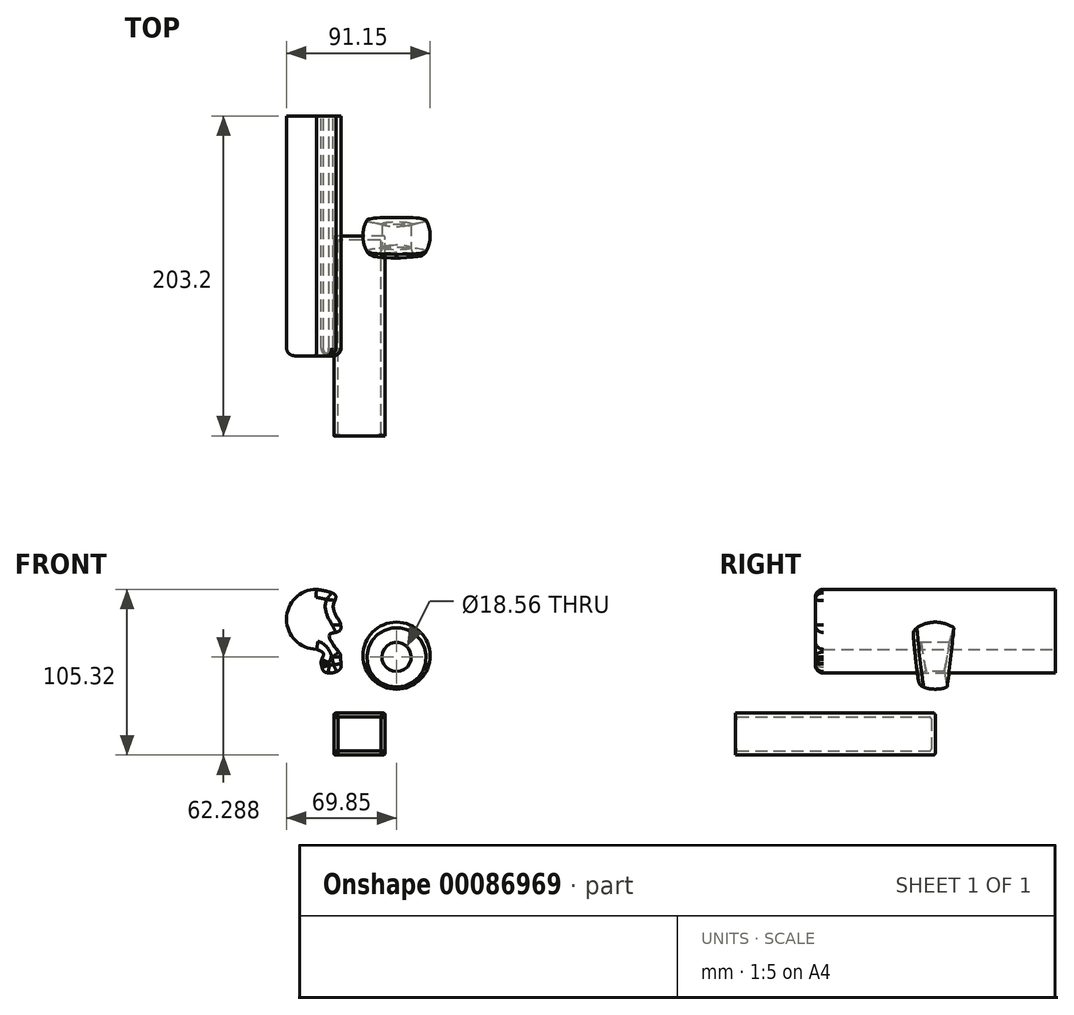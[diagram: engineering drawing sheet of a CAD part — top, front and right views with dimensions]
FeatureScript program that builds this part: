
annotation { "Feature Type Name" : "Feature", "Feature Type Description" : "" }
export const myFeature = defineFeature(function(context is Context, id is Id, definition is map)
    precondition{}
    {
        {
            var Q0;
            Q0=qCreatedBy(makeId("Front.planeOp"),FACE);
            var sketch = newSketch(context, id + "F0", { "sketchPlane" : qUnion([Q0])});
            skLineSegment(sketch, "E0", {"start": v(0, 0) * mm, "end": v(0, 42.6) * mm});
            skArc(sketch, "E1", {"start": v(0, 42.6) * mm, "mid": v(-21.3, 21.3) * mm, "end": v(0, 0) * mm});
            skSolve(sketch);
        }
        {
            var Q0;
            Q0 = qSketchRegion(id + "F0", true);
            var Q1;
            Q1=sQuery(id+"F0.wireOp",EDGE,"E0");
            revolve(context, id + "F1", {"entities" : qUnion([Q0]), "axis" : qUnion([Q1]), "revolveType" : RevolveType.FULL});
        }
        {
            var Q0;
            Q0=qCreatedBy(makeId("Front.planeOp"),FACE);
            var sketch = newSketch(context, id + "F2", { "sketchPlane" : qUnion([Q0])});
            skCircle(sketch, "E2", {"center": v(0, 20.47) * mm, "radius": 9.28 * mm});
            skSolve(sketch);
        }
        {
            var Q0;
            Q0 = qSketchRegion(id + "F2", true);
            extrude(context, id + "F3", {"entities" : qUnion([Q0]), "operationType" : NewBodyOperationType.REMOVE, "endBound" : BoundingType.SYMMETRIC, "oppositeDirection" : true, "depth" : 92.12 * mm});
        }
        {
            var Q0;
            Q0=qCreatedBy(makeId("Front.planeOp"),FACE);
            var sketch = newSketch(context, id + "F4", { "sketchPlane" : qUnion([Q0])});
            skArc(sketch, "E3", {"start": v(-50.8, 63.5) * mm, "mid": v(-69.85, 44.45) * mm, "end": v(-50.8, 25.4) * mm});
            skLineSegment(sketch, "E4", {"start": v(-50.8, 63.5) * mm, "end": v(-50.8, 25.4) * mm, "construction": true});
            skFitSpline(sketch, "E5", {"points": [v(-50.8, 63.5) * mm, v(-38.58, 59.25) * mm, v(-40.15, 53.18) * mm, v(-37.21, 44.75) * mm, v(-35.65, 41.62) * mm, v(-35.65, 37.7) * mm, v(-39.37, 35.94) * mm, v(-42.7, 34.18) * mm, v(-38, 25.36) * mm, v(-35.65, 22.03) * mm, v(-35.45, 18.5) * mm, v(-35.45, 13.42) * mm, v(-40.35, 10.48) * mm, v(-46.03, 11.26) * mm, v(-47.4, 14.2) * mm, v(-47.8, 18.12) * mm, v(-46.42, 22.43) * mm, v(-50.8, 25.4) * mm], "startDerivative": vector(187.17, -33.7) * mm, "endDerivative": vector(-104.87, 42.61) * mm});
            skSolve(sketch);
        }
        {
            var Q0;
            Q0 = qSketchRegion(id + "F4", true);
            extrude(context, id + "F5", {"entities" : qUnion([Q0]), "endBound" : BoundingType.SYMMETRIC, "depth" : 152.4 * mm});
        }
        {
            var Q0;
            Q0=makeQuery(id+"F5.opExtrude","CAP_EDGE",EDGE,{"disambiguationData":[OSD([sQuery(id+"F4.wireOp",EDGE,"E3")])],"isStart":false});
            var Q1;
            Q1=makeQuery(id+"F5.opExtrude","CAP_EDGE",EDGE,{"disambiguationData":[OSD([sQuery(id+"F4.wireOp",EDGE,"E5")])],"isStart":false});
            fillet(context, id + "F6", {"entities" : qUnion([Q0, Q1]), "radius" : 5.08 * mm, "tangentPropagation" : true, "allowEdgeOverflow" : false});
        }
        {
            var Q0;
            Q0=makeQuery(id+"F3.boolean.opBoolean","INTERSECT",EDGE,{"disambiguationData":[OD(1.0)],"derivedFrom":[makeQuery(id+"F1.opRevolve","SWEPT_FACE",FACE,{"disambiguationData":[OSD([sQuery(id+"F0.wireOp",EDGE,"E1")])]}),makeQuery(id+"F3.opExtrude","SWEPT_FACE",FACE,{"disambiguationData":[OSD([sQuery(id+"F2.wireOp",EDGE,"E2")])]})]});
            chamfer(context, id + "F7", {"entities" : qUnion([Q0]), "width" : 5.08 * mm, "tangentPropagation" : true});
        }
        {
            var Q0;
            Q0=makeQuery(id+"F3.boolean.opBoolean","INTERSECT",EDGE,{"disambiguationData":[OD(0.0)],"derivedFrom":[makeQuery(id+"F1.opRevolve","SWEPT_FACE",FACE,{"disambiguationData":[OSD([sQuery(id+"F0.wireOp",EDGE,"E1")])]}),makeQuery(id+"F3.opExtrude","SWEPT_FACE",FACE,{"disambiguationData":[OSD([sQuery(id+"F2.wireOp",EDGE,"E2")])]})]});
            fillet(context, id + "F8", {"entities" : qUnion([Q0]), "radius" : 5.08 * mm, "tangentPropagation" : true, "allowEdgeOverflow" : false});
        }
        {
            var Q0;
            Q0=qCreatedBy(makeId("Front.planeOp"),FACE);
            var sketch = newSketch(context, id + "F9", { "sketchPlane" : qUnion([Q0])});
            skLineSegment(sketch, "E6.bottom", {"start": v(-7.25, -15.18) * mm, "end": v(-39.76, -15.18) * mm});
            skLineSegment(sketch, "E6.top", {"start": v(-7.25, -41.82) * mm, "end": v(-39.76, -41.82) * mm});
            skLineSegment(sketch, "E6.left", {"start": v(-7.25, -15.18) * mm, "end": v(-7.25, -41.82) * mm});
            skLineSegment(sketch, "E6.right", {"start": v(-39.76, -15.18) * mm, "end": v(-39.76, -41.82) * mm});
            skPoint(sketch, "E6.middle", {"position": v(-23.5, -28.5) * mm});
            skSolve(sketch);
        }
        {
            var Q0;
            Q0 = qSketchRegion(id + "F9", true);
            extrude(context, id + "F10", {"entities" : qUnion([Q0]), "depth" : 127 * mm});
        }
        {
            var Q0;
            Q0=makeQuery(id+"F10.opExtrude","CAP_FACE",FACE,{"disambiguationData":[OSD([sQuery(id+"F9.wireOp",EDGE,"E6.bottom"),sQuery(id+"F9.wireOp",EDGE,"E6.top"),sQuery(id+"F9.wireOp",EDGE,"E6.left"),sQuery(id+"F9.wireOp",EDGE,"E6.right")])],"isStart":false});
            shell(context, id + "F11", {"entities" : qUnion([Q0]), "thickness" : 2.54 * mm});
        }
        {
            var Q0;
            Q0=makeQuery(id+"F10.opExtrude","SWEPT_EDGE",EDGE,{"disambiguationData":[OSD([sQuery(id+"F9.wireOp",EDGE,"E6.bottom"),sQuery(id+"F9.wireOp",EDGE,"E6.right")])]});
            var Q1;
            Q1=makeQuery(id+"F10.opExtrude","SWEPT_EDGE",EDGE,{"disambiguationData":[OSD([sQuery(id+"F9.wireOp",EDGE,"E6.top"),sQuery(id+"F9.wireOp",EDGE,"E6.right")])]});
            var Q2;
            Q2=makeQuery(id+"F10.opExtrude","SWEPT_EDGE",EDGE,{"disambiguationData":[OSD([sQuery(id+"F9.wireOp",EDGE,"E6.top"),sQuery(id+"F9.wireOp",EDGE,"E6.left")])]});
            var Q3;
            Q3=makeQuery(id+"F10.opExtrude","SWEPT_EDGE",EDGE,{"disambiguationData":[OSD([sQuery(id+"F9.wireOp",EDGE,"E6.bottom"),sQuery(id+"F9.wireOp",EDGE,"E6.left")])]});
            var Q4;
            {var subQ0=sQuery(id+"F9.wireOp",EDGE,"E6.right");Q4=makeQuery(id+"F11.opShell","OFFSET_EDGE",EDGE,{"disambiguationData":[OSD([subQ0]),TDD([makeQuery(id+"F10.opExtrude","CAP_EDGE",EDGE,{"disambiguationData":[OSD([subQ0])],"isStart":false})])]});}
            var Q5;
            {var subQ0=sQuery(id+"F9.wireOp",EDGE,"E6.top");Q5=makeQuery(id+"F11.opShell","OFFSET_EDGE",EDGE,{"disambiguationData":[OSD([subQ0]),TDD([makeQuery(id+"F10.opExtrude","CAP_EDGE",EDGE,{"disambiguationData":[OSD([subQ0])],"isStart":false})])]});}
            var Q6;
            {var subQ0=sQuery(id+"F9.wireOp",EDGE,"E6.bottom");Q6=makeQuery(id+"F11.opShell","OFFSET_EDGE",EDGE,{"disambiguationData":[OSD([subQ0]),TDD([makeQuery(id+"F10.opExtrude","CAP_EDGE",EDGE,{"disambiguationData":[OSD([subQ0])],"isStart":false})])]});}
            var Q7;
            {var subQ0=sQuery(id+"F9.wireOp",EDGE,"E6.left");Q7=makeQuery(id+"F11.opShell","OFFSET_EDGE",EDGE,{"disambiguationData":[OSD([subQ0]),TDD([makeQuery(id+"F10.opExtrude","CAP_EDGE",EDGE,{"disambiguationData":[OSD([subQ0])],"isStart":false})])]});}
            fillet(context, id + "F12", {"entities" : qUnion([Q0, Q1, Q2, Q3, Q4, Q5, Q6, Q7]), "radius" : 1.27 * mm, "tangentPropagation" : true, "allowEdgeOverflow" : false});
        }
        {
            var Q0;
            Q0=makeQuery(id+"F11.opShell","OFFSET_FACE",FACE,{"disambiguationData":[OSD([sQuery(id+"F9.wireOp",EDGE,"E6.right")])]});
            var Q1;
            Q1=makeQuery(id+"F11.opShell","OFFSET_FACE",FACE,{"disambiguationData":[OSD([sQuery(id+"F9.wireOp",EDGE,"E6.bottom")])]});
            var Q2;
            Q2=makeQuery(id+"F11.opShell","OFFSET_FACE",FACE,{"disambiguationData":[OSD([sQuery(id+"F9.wireOp",EDGE,"E6.left")])]});
            var Q3;
            Q3=makeQuery(id+"F10.opExtrude","CAP_FACE",FACE,{"disambiguationData":[OSD([sQuery(id+"F9.wireOp",EDGE,"E6.bottom"),sQuery(id+"F9.wireOp",EDGE,"E6.top"),sQuery(id+"F9.wireOp",EDGE,"E6.left"),sQuery(id+"F9.wireOp",EDGE,"E6.right")])],"isStart":true});
            fillet(context, id + "F13", {"entities" : qUnion([Q0, Q1, Q2, Q3]), "radius" : 1.27 * mm, "tangentPropagation" : true, "allowEdgeOverflow" : false});
        }
        {
            var Q0;
            Q0=makeQuery(id+"F11.opShell","OFFSET_FACE",FACE,{"disambiguationData":[OSD([sQuery(id+"F9.wireOp",EDGE,"E6.bottom"),sQuery(id+"F9.wireOp",EDGE,"E6.top"),sQuery(id+"F9.wireOp",EDGE,"E6.left"),sQuery(id+"F9.wireOp",EDGE,"E6.right")])]});
            fillet(context, id + "F14", {"entities" : qUnion([Q0]), "radius" : 1.27 * mm, "tangentPropagation" : true, "allowEdgeOverflow" : false});
        }
    });
